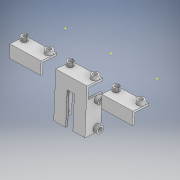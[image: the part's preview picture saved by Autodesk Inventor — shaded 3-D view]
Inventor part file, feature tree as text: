
AUTODESK INVENTOR PART (.ipt)
format: ipt  version: 2020 (Build 240168000, 168)  size: 192,000 bytes
history: native  units: mm
features: other x6, sketch x5
ambient origin geometry x8: Origin, YZ Plane, XZ Plane, XY Plane, X Axis, Y Axis, Z Axis, Center Point
bodies: Solid1 (feature_tree)
feature tree (11):
  other  "5DržačaLidara.iam"
  other  "DržačSenzoraUdaljenostiOnlyOne(1)_v.1.0.ipt:1"
  other  "DržačSenzoraUdaljenostiOnlyOne(1)_v.1.0.ipt:2"
  other  "DržačSenzoraUdaljenostiOnlyOne(1)_v.1.0.ipt:3"
  other  "DržačSenzoraUdaljenostiOnlyOne(1)_v.1.0.ipt:4"
  other  "DržačSenzoraUdaljenostiOnlyOne(1)_v.1.0.ipt:5"
  sketch  "Sketch8"
  sketch  "Sketch8_1"  dims[d0=10.0mm]
  sketch  "Sketch8_2"
  sketch  "Sketch8_3"
  sketch  "Sketch8_4"
